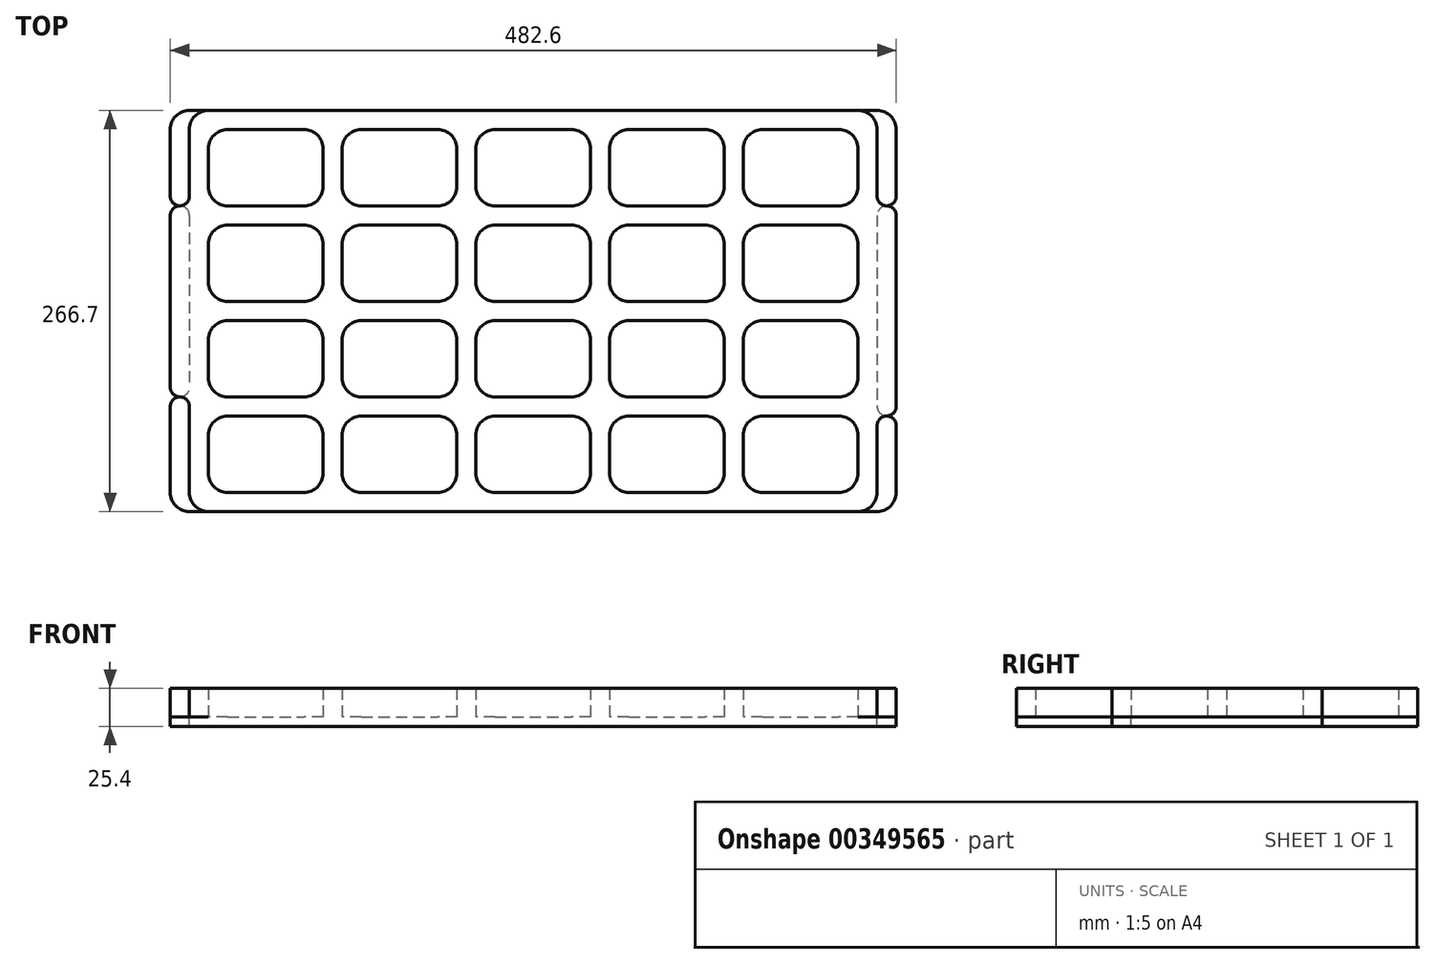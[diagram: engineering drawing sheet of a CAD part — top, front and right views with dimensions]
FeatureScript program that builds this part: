
annotation { "Feature Type Name" : "Feature", "Feature Type Description" : "" }
export const myFeature = defineFeature(function(context is Context, id is Id, definition is map)
    precondition{}
    {
        {
            var Q0;
            Q0=qCreatedBy(makeId("Top.planeOp"),FACE);
            var sketch = newSketch(context, id + "F0", { "sketchPlane" : qUnion([Q0])});
            skLineSegment(sketch, "E0.bottom", {"start": v(0, 0) * mm, "end": v(76.2, 0) * mm});
            skLineSegment(sketch, "E0.top", {"start": v(0, 50.8) * mm, "end": v(76.2, 50.8) * mm});
            skLineSegment(sketch, "E0.left", {"start": v(0, 0) * mm, "end": v(0, 50.8) * mm});
            skLineSegment(sketch, "E0.right", {"start": v(76.2, 0) * mm, "end": v(76.2, 50.8) * mm});
            skLineSegment(sketch, "E1.0.1.0", {"start": v(0, 114.3) * mm, "end": v(76.2, 114.3) * mm});
            skLineSegment(sketch, "E1.0.1.1", {"start": v(0, 63.5) * mm, "end": v(0, 114.3) * mm});
            skLineSegment(sketch, "E1.0.1.2", {"start": v(76.2, 63.5) * mm, "end": v(76.2, 114.3) * mm});
            skLineSegment(sketch, "E1.0.1.3", {"start": v(0, 63.5) * mm, "end": v(76.2, 63.5) * mm});
            skLineSegment(sketch, "E1.0.2.0", {"start": v(0, 177.8) * mm, "end": v(76.2, 177.8) * mm});
            skLineSegment(sketch, "E1.0.2.1", {"start": v(0, 127) * mm, "end": v(0, 177.8) * mm});
            skLineSegment(sketch, "E1.0.2.2", {"start": v(76.2, 127) * mm, "end": v(76.2, 177.8) * mm});
            skLineSegment(sketch, "E1.0.2.3", {"start": v(0, 127) * mm, "end": v(76.2, 127) * mm});
            skLineSegment(sketch, "E1.0.3.0", {"start": v(0, 241.3) * mm, "end": v(76.2, 241.3) * mm});
            skLineSegment(sketch, "E1.0.3.1", {"start": v(0, 190.5) * mm, "end": v(0, 241.3) * mm});
            skLineSegment(sketch, "E1.0.3.2", {"start": v(76.2, 190.5) * mm, "end": v(76.2, 241.3) * mm});
            skLineSegment(sketch, "E1.0.3.3", {"start": v(0, 190.5) * mm, "end": v(76.2, 190.5) * mm});
            skLineSegment(sketch, "E1.1.0.0", {"start": v(88.9, 50.8) * mm, "end": v(165.1, 50.8) * mm});
            skLineSegment(sketch, "E1.1.0.1", {"start": v(88.9, 0) * mm, "end": v(88.9, 50.8) * mm});
            skLineSegment(sketch, "E1.1.0.2", {"start": v(165.1, 0) * mm, "end": v(165.1, 50.8) * mm});
            skLineSegment(sketch, "E1.1.0.3", {"start": v(88.9, 0) * mm, "end": v(165.1, 0) * mm});
            skLineSegment(sketch, "E1.1.1.0", {"start": v(88.9, 114.3) * mm, "end": v(165.1, 114.3) * mm});
            skLineSegment(sketch, "E1.1.1.1", {"start": v(88.9, 63.5) * mm, "end": v(88.9, 114.3) * mm});
            skLineSegment(sketch, "E1.1.1.2", {"start": v(165.1, 63.5) * mm, "end": v(165.1, 114.3) * mm});
            skLineSegment(sketch, "E1.1.1.3", {"start": v(88.9, 63.5) * mm, "end": v(165.1, 63.5) * mm});
            skLineSegment(sketch, "E1.1.2.0", {"start": v(88.9, 177.8) * mm, "end": v(165.1, 177.8) * mm});
            skLineSegment(sketch, "E1.1.2.1", {"start": v(88.9, 127) * mm, "end": v(88.9, 177.8) * mm});
            skLineSegment(sketch, "E1.1.2.2", {"start": v(165.1, 127) * mm, "end": v(165.1, 177.8) * mm});
            skLineSegment(sketch, "E1.1.2.3", {"start": v(88.9, 127) * mm, "end": v(165.1, 127) * mm});
            skLineSegment(sketch, "E1.1.3.0", {"start": v(88.9, 241.3) * mm, "end": v(165.1, 241.3) * mm});
            skLineSegment(sketch, "E1.1.3.1", {"start": v(88.9, 190.5) * mm, "end": v(88.9, 241.3) * mm});
            skLineSegment(sketch, "E1.1.3.2", {"start": v(165.1, 190.5) * mm, "end": v(165.1, 241.3) * mm});
            skLineSegment(sketch, "E1.1.3.3", {"start": v(88.9, 190.5) * mm, "end": v(165.1, 190.5) * mm});
            skLineSegment(sketch, "E1.2.0.0", {"start": v(177.8, 50.8) * mm, "end": v(254, 50.8) * mm});
            skLineSegment(sketch, "E1.2.0.1", {"start": v(177.8, 0) * mm, "end": v(177.8, 50.8) * mm});
            skLineSegment(sketch, "E1.2.0.2", {"start": v(254, 0) * mm, "end": v(254, 50.8) * mm});
            skLineSegment(sketch, "E1.2.0.3", {"start": v(177.8, 0) * mm, "end": v(254, 0) * mm});
            skLineSegment(sketch, "E1.2.1.0", {"start": v(177.8, 114.3) * mm, "end": v(254, 114.3) * mm});
            skLineSegment(sketch, "E1.2.1.1", {"start": v(177.8, 63.5) * mm, "end": v(177.8, 114.3) * mm});
            skLineSegment(sketch, "E1.2.1.2", {"start": v(254, 63.5) * mm, "end": v(254, 114.3) * mm});
            skLineSegment(sketch, "E1.2.1.3", {"start": v(177.8, 63.5) * mm, "end": v(254, 63.5) * mm});
            skLineSegment(sketch, "E1.2.2.0", {"start": v(177.8, 177.8) * mm, "end": v(254, 177.8) * mm});
            skLineSegment(sketch, "E1.2.2.1", {"start": v(177.8, 127) * mm, "end": v(177.8, 177.8) * mm});
            skLineSegment(sketch, "E1.2.2.2", {"start": v(254, 127) * mm, "end": v(254, 177.8) * mm});
            skLineSegment(sketch, "E1.2.2.3", {"start": v(177.8, 127) * mm, "end": v(254, 127) * mm});
            skLineSegment(sketch, "E1.2.3.0", {"start": v(177.8, 241.3) * mm, "end": v(254, 241.3) * mm});
            skLineSegment(sketch, "E1.2.3.1", {"start": v(177.8, 190.5) * mm, "end": v(177.8, 241.3) * mm});
            skLineSegment(sketch, "E1.2.3.2", {"start": v(254, 190.5) * mm, "end": v(254, 241.3) * mm});
            skLineSegment(sketch, "E1.2.3.3", {"start": v(177.8, 190.5) * mm, "end": v(254, 190.5) * mm});
            skLineSegment(sketch, "E1.3.0.0", {"start": v(266.7, 50.8) * mm, "end": v(342.9, 50.8) * mm});
            skLineSegment(sketch, "E1.3.0.1", {"start": v(266.7, 0) * mm, "end": v(266.7, 50.8) * mm});
            skLineSegment(sketch, "E1.3.0.2", {"start": v(342.9, 0) * mm, "end": v(342.9, 50.8) * mm});
            skLineSegment(sketch, "E1.3.0.3", {"start": v(266.7, 0) * mm, "end": v(342.9, 0) * mm});
            skLineSegment(sketch, "E1.3.1.0", {"start": v(266.7, 114.3) * mm, "end": v(342.9, 114.3) * mm});
            skLineSegment(sketch, "E1.3.1.1", {"start": v(266.7, 63.5) * mm, "end": v(266.7, 114.3) * mm});
            skLineSegment(sketch, "E1.3.1.2", {"start": v(342.9, 63.5) * mm, "end": v(342.9, 114.3) * mm});
            skLineSegment(sketch, "E1.3.1.3", {"start": v(266.7, 63.5) * mm, "end": v(342.9, 63.5) * mm});
            skLineSegment(sketch, "E1.3.2.0", {"start": v(266.7, 177.8) * mm, "end": v(342.9, 177.8) * mm});
            skLineSegment(sketch, "E1.3.2.1", {"start": v(266.7, 127) * mm, "end": v(266.7, 177.8) * mm});
            skLineSegment(sketch, "E1.3.2.2", {"start": v(342.9, 127) * mm, "end": v(342.9, 177.8) * mm});
            skLineSegment(sketch, "E1.3.2.3", {"start": v(266.7, 127) * mm, "end": v(342.9, 127) * mm});
            skLineSegment(sketch, "E1.3.3.0", {"start": v(266.7, 241.3) * mm, "end": v(342.9, 241.3) * mm});
            skLineSegment(sketch, "E1.3.3.1", {"start": v(266.7, 190.5) * mm, "end": v(266.7, 241.3) * mm});
            skLineSegment(sketch, "E1.3.3.2", {"start": v(342.9, 190.5) * mm, "end": v(342.9, 241.3) * mm});
            skLineSegment(sketch, "E1.3.3.3", {"start": v(266.7, 190.5) * mm, "end": v(342.9, 190.5) * mm});
            skLineSegment(sketch, "E1.4.0.0", {"start": v(355.6, 50.8) * mm, "end": v(431.8, 50.8) * mm});
            skLineSegment(sketch, "E1.4.0.1", {"start": v(355.6, 0) * mm, "end": v(355.6, 50.8) * mm});
            skLineSegment(sketch, "E1.4.0.2", {"start": v(431.8, 0) * mm, "end": v(431.8, 50.8) * mm});
            skLineSegment(sketch, "E1.4.0.3", {"start": v(355.6, 0) * mm, "end": v(431.8, 0) * mm});
            skLineSegment(sketch, "E1.4.1.0", {"start": v(355.6, 114.3) * mm, "end": v(431.8, 114.3) * mm});
            skLineSegment(sketch, "E1.4.1.1", {"start": v(355.6, 63.5) * mm, "end": v(355.6, 114.3) * mm});
            skLineSegment(sketch, "E1.4.1.2", {"start": v(431.8, 63.5) * mm, "end": v(431.8, 114.3) * mm});
            skLineSegment(sketch, "E1.4.1.3", {"start": v(355.6, 63.5) * mm, "end": v(431.8, 63.5) * mm});
            skLineSegment(sketch, "E1.4.2.0", {"start": v(355.6, 177.8) * mm, "end": v(431.8, 177.8) * mm});
            skLineSegment(sketch, "E1.4.2.1", {"start": v(355.6, 127) * mm, "end": v(355.6, 177.8) * mm});
            skLineSegment(sketch, "E1.4.2.2", {"start": v(431.8, 127) * mm, "end": v(431.8, 177.8) * mm});
            skLineSegment(sketch, "E1.4.2.3", {"start": v(355.6, 127) * mm, "end": v(431.8, 127) * mm});
            skLineSegment(sketch, "E1.4.3.0", {"start": v(355.6, 241.3) * mm, "end": v(431.8, 241.3) * mm});
            skLineSegment(sketch, "E1.4.3.1", {"start": v(355.6, 190.5) * mm, "end": v(355.6, 241.3) * mm});
            skLineSegment(sketch, "E1.4.3.2", {"start": v(431.8, 190.5) * mm, "end": v(431.8, 241.3) * mm});
            skLineSegment(sketch, "E1.4.3.3", {"start": v(355.6, 190.5) * mm, "end": v(431.8, 190.5) * mm});
            skLineSegment(sketch, "E1.direction1", {"start": v(0, 0) * mm, "end": v(88.9, 0) * mm, "construction": true});
            skLineSegment(sketch, "E1.direction2", {"start": v(0, 0) * mm, "end": v(0, 63.5) * mm, "construction": true});
            skLineSegment(sketch, "E2.bottom", {"start": v(-12.7, 254) * mm, "end": v(444.5, 254) * mm});
            skLineSegment(sketch, "E2.top", {"start": v(-12.7, -12.7) * mm, "end": v(444.5, -12.7) * mm});
            skLineSegment(sketch, "E2.left", {"start": v(-12.7, 254) * mm, "end": v(-12.7, -12.7) * mm});
            skLineSegment(sketch, "E3", {"start": v(444.5, -12.7) * mm, "end": v(444.5, 254) * mm});
            skArc(sketch, "E4", {"start": v(450.85, 50.8) * mm, "mid": v(446.36, 48.94) * mm, "end": v(444.5, 44.45) * mm});
            skArc(sketch, "E5", {"start": v(444.5, 196.85) * mm, "mid": v(446.36, 192.36) * mm, "end": v(450.85, 190.5) * mm});
            skArc(sketch, "E6", {"start": v(457.2, 184.15) * mm, "mid": v(455.34, 188.64) * mm, "end": v(450.85, 190.5) * mm});
            skArc(sketch, "E7", {"start": v(450.85, 50.8) * mm, "mid": v(455.34, 52.66) * mm, "end": v(457.2, 57.15) * mm});
            skLineSegment(sketch, "E8", {"start": v(457.2, 184.15) * mm, "end": v(457.2, 57.15) * mm});
            skArc(sketch, "E9", {"start": v(-19.05, 190.5) * mm, "mid": v(-14.56, 192.36) * mm, "end": v(-12.7, 196.85) * mm});
            skArc(sketch, "E10", {"start": v(-19.05, 190.5) * mm, "mid": v(-23.54, 188.64) * mm, "end": v(-25.4, 184.15) * mm});
            skArc(sketch, "E11", {"start": v(-25.4, 69.85) * mm, "mid": v(-23.54, 65.36) * mm, "end": v(-19.05, 63.5) * mm});
            skArc(sketch, "E12", {"start": v(-12.7, 57.15) * mm, "mid": v(-14.56, 61.64) * mm, "end": v(-19.05, 63.5) * mm});
            skLineSegment(sketch, "E13", {"start": v(-25.4, 184.15) * mm, "end": v(-25.4, 69.85) * mm});
            skSolve(sketch);
        }
        {
            var Q0;
            Q0 = qSketchRegion(id + "F0", true);
            extrude(context, id + "F1", {"entities" : qUnion([Q0]), "depth" : 19.05 * mm});
        }
        {
            var Q0;
            Q0=makeQuery(id+"F1.opExtrude","SWEPT_EDGE",EDGE,{"disambiguationData":[OSD([sQuery(id+"F0.wireOp",EDGE,"E1.4.3.2"),sQuery(id+"F0.wireOp",EDGE,"E1.4.3.3")])]});
            var Q1;
            Q1=makeQuery(id+"F1.opExtrude","SWEPT_EDGE",EDGE,{"disambiguationData":[OSD([sQuery(id+"F0.wireOp",EDGE,"E1.4.2.2"),sQuery(id+"F0.wireOp",EDGE,"E1.4.2.3")])]});
            var Q2;
            Q2=makeQuery(id+"F1.opExtrude","SWEPT_EDGE",EDGE,{"disambiguationData":[OSD([sQuery(id+"F0.wireOp",EDGE,"E1.4.1.2"),sQuery(id+"F0.wireOp",EDGE,"E1.4.1.3")])]});
            var Q3;
            Q3=makeQuery(id+"F1.opExtrude","SWEPT_EDGE",EDGE,{"disambiguationData":[OSD([sQuery(id+"F0.wireOp",EDGE,"E1.4.0.2"),sQuery(id+"F0.wireOp",EDGE,"E1.4.0.3")])]});
            var Q4;
            Q4=makeQuery(id+"F1.opExtrude","SWEPT_EDGE",EDGE,{"disambiguationData":[OSD([sQuery(id+"F0.wireOp",EDGE,"E2.bottom"),sQuery(id+"F0.wireOp",EDGE,"E2.left")])]});
            var Q5;
            Q5=makeQuery(id+"F1.opExtrude","SWEPT_EDGE",EDGE,{"disambiguationData":[OSD([sQuery(id+"F0.wireOp",EDGE,"E1.0.3.2"),sQuery(id+"F0.wireOp",EDGE,"E1.0.3.3")])]});
            var Q6;
            Q6=makeQuery(id+"F1.opExtrude","SWEPT_EDGE",EDGE,{"disambiguationData":[OSD([sQuery(id+"F0.wireOp",EDGE,"E1.1.3.2"),sQuery(id+"F0.wireOp",EDGE,"E1.1.3.3")])]});
            var Q7;
            Q7=makeQuery(id+"F1.opExtrude","SWEPT_EDGE",EDGE,{"disambiguationData":[OSD([sQuery(id+"F0.wireOp",EDGE,"E1.2.3.2"),sQuery(id+"F0.wireOp",EDGE,"E1.2.3.3")])]});
            var Q8;
            Q8=makeQuery(id+"F1.opExtrude","SWEPT_EDGE",EDGE,{"disambiguationData":[OSD([sQuery(id+"F0.wireOp",EDGE,"E1.3.1.2"),sQuery(id+"F0.wireOp",EDGE,"E1.3.1.3")])]});
            var Q9;
            Q9=makeQuery(id+"F1.opExtrude","SWEPT_EDGE",EDGE,{"disambiguationData":[OSD([sQuery(id+"F0.wireOp",EDGE,"E1.3.0.2"),sQuery(id+"F0.wireOp",EDGE,"E1.3.0.3")])]});
            var Q10;
            Q10=makeQuery(id+"F1.opExtrude","SWEPT_EDGE",EDGE,{"disambiguationData":[OSD([sQuery(id+"F0.wireOp",EDGE,"E1.3.2.2"),sQuery(id+"F0.wireOp",EDGE,"E1.3.2.3")])]});
            var Q11;
            Q11=makeQuery(id+"F1.opExtrude","SWEPT_EDGE",EDGE,{"disambiguationData":[OSD([sQuery(id+"F0.wireOp",EDGE,"E1.3.3.2"),sQuery(id+"F0.wireOp",EDGE,"E1.3.3.3")])]});
            var Q12;
            Q12=makeQuery(id+"F1.opExtrude","SWEPT_EDGE",EDGE,{"disambiguationData":[OSD([sQuery(id+"F0.wireOp",EDGE,"E1.2.2.2"),sQuery(id+"F0.wireOp",EDGE,"E1.2.2.3")])]});
            var Q13;
            Q13=makeQuery(id+"F1.opExtrude","SWEPT_EDGE",EDGE,{"disambiguationData":[OSD([sQuery(id+"F0.wireOp",EDGE,"E1.2.1.2"),sQuery(id+"F0.wireOp",EDGE,"E1.2.1.3")])]});
            var Q14;
            Q14=makeQuery(id+"F1.opExtrude","SWEPT_EDGE",EDGE,{"disambiguationData":[OSD([sQuery(id+"F0.wireOp",EDGE,"E1.2.0.2"),sQuery(id+"F0.wireOp",EDGE,"E1.2.0.3")])]});
            var Q15;
            Q15=makeQuery(id+"F1.opExtrude","SWEPT_EDGE",EDGE,{"disambiguationData":[OSD([sQuery(id+"F0.wireOp",EDGE,"E1.1.0.2"),sQuery(id+"F0.wireOp",EDGE,"E1.1.0.3")])]});
            var Q16;
            Q16=makeQuery(id+"F1.opExtrude","SWEPT_EDGE",EDGE,{"disambiguationData":[OSD([sQuery(id+"F0.wireOp",EDGE,"E1.1.1.2"),sQuery(id+"F0.wireOp",EDGE,"E1.1.1.3")])]});
            var Q17;
            Q17=makeQuery(id+"F1.opExtrude","SWEPT_EDGE",EDGE,{"disambiguationData":[OSD([sQuery(id+"F0.wireOp",EDGE,"E1.1.2.2"),sQuery(id+"F0.wireOp",EDGE,"E1.1.2.3")])]});
            var Q18;
            Q18=makeQuery(id+"F1.opExtrude","SWEPT_EDGE",EDGE,{"disambiguationData":[OSD([sQuery(id+"F0.wireOp",EDGE,"E1.0.2.2"),sQuery(id+"F0.wireOp",EDGE,"E1.0.2.3")])]});
            var Q19;
            Q19=makeQuery(id+"F1.opExtrude","SWEPT_EDGE",EDGE,{"disambiguationData":[OSD([sQuery(id+"F0.wireOp",EDGE,"E1.0.1.2"),sQuery(id+"F0.wireOp",EDGE,"E1.0.1.3")])]});
            var Q20;
            Q20=makeQuery(id+"F1.opExtrude","SWEPT_EDGE",EDGE,{"disambiguationData":[OSD([sQuery(id+"F0.wireOp",EDGE,"E0.bottom"),sQuery(id+"F0.wireOp",EDGE,"E0.right")])]});
            var Q21;
            Q21=makeQuery(id+"F1.opExtrude","SWEPT_EDGE",EDGE,{"disambiguationData":[OSD([sQuery(id+"F0.wireOp",EDGE,"E1.4.0.1"),sQuery(id+"F0.wireOp",EDGE,"E1.4.0.3")])]});
            var Q22;
            Q22=makeQuery(id+"F1.opExtrude","SWEPT_EDGE",EDGE,{"disambiguationData":[OSD([sQuery(id+"F0.wireOp",EDGE,"E2.top"),sQuery(id+"F0.wireOp",EDGE,"E3")])]});
            var Q23;
            Q23=makeQuery(id+"F1.opExtrude","SWEPT_EDGE",EDGE,{"disambiguationData":[OSD([sQuery(id+"F0.wireOp",EDGE,"E2.bottom"),sQuery(id+"F0.wireOp",EDGE,"E3")])]});
            var Q24;
            Q24=makeQuery(id+"F1.opExtrude","SWEPT_EDGE",EDGE,{"disambiguationData":[OSD([sQuery(id+"F0.wireOp",EDGE,"E1.4.2.1"),sQuery(id+"F0.wireOp",EDGE,"E1.4.2.3")])]});
            var Q25;
            Q25=makeQuery(id+"F1.opExtrude","SWEPT_EDGE",EDGE,{"disambiguationData":[OSD([sQuery(id+"F0.wireOp",EDGE,"E1.4.1.1"),sQuery(id+"F0.wireOp",EDGE,"E1.4.1.3")])]});
            var Q26;
            Q26=makeQuery(id+"F1.opExtrude","SWEPT_EDGE",EDGE,{"disambiguationData":[OSD([sQuery(id+"F0.wireOp",EDGE,"E1.3.0.1"),sQuery(id+"F0.wireOp",EDGE,"E1.3.0.3")])]});
            var Q27;
            Q27=makeQuery(id+"F1.opExtrude","SWEPT_EDGE",EDGE,{"disambiguationData":[OSD([sQuery(id+"F0.wireOp",EDGE,"E1.3.1.1"),sQuery(id+"F0.wireOp",EDGE,"E1.3.1.3")])]});
            var Q28;
            Q28=makeQuery(id+"F1.opExtrude","SWEPT_EDGE",EDGE,{"disambiguationData":[OSD([sQuery(id+"F0.wireOp",EDGE,"E1.4.3.1"),sQuery(id+"F0.wireOp",EDGE,"E1.4.3.3")])]});
            var Q29;
            Q29=makeQuery(id+"F1.opExtrude","SWEPT_EDGE",EDGE,{"disambiguationData":[OSD([sQuery(id+"F0.wireOp",EDGE,"E1.2.0.1"),sQuery(id+"F0.wireOp",EDGE,"E1.2.0.3")])]});
            var Q30;
            Q30=makeQuery(id+"F1.opExtrude","SWEPT_EDGE",EDGE,{"disambiguationData":[OSD([sQuery(id+"F0.wireOp",EDGE,"E1.2.1.1"),sQuery(id+"F0.wireOp",EDGE,"E1.2.1.3")])]});
            var Q31;
            Q31=makeQuery(id+"F1.opExtrude","SWEPT_EDGE",EDGE,{"disambiguationData":[OSD([sQuery(id+"F0.wireOp",EDGE,"E1.2.2.1"),sQuery(id+"F0.wireOp",EDGE,"E1.2.2.3")])]});
            var Q32;
            Q32=makeQuery(id+"F1.opExtrude","SWEPT_EDGE",EDGE,{"disambiguationData":[OSD([sQuery(id+"F0.wireOp",EDGE,"E1.3.2.1"),sQuery(id+"F0.wireOp",EDGE,"E1.3.2.3")])]});
            var Q33;
            Q33=makeQuery(id+"F1.opExtrude","SWEPT_EDGE",EDGE,{"disambiguationData":[OSD([sQuery(id+"F0.wireOp",EDGE,"E1.3.3.1"),sQuery(id+"F0.wireOp",EDGE,"E1.3.3.3")])]});
            var Q34;
            Q34=makeQuery(id+"F1.opExtrude","SWEPT_EDGE",EDGE,{"disambiguationData":[OSD([sQuery(id+"F0.wireOp",EDGE,"E1.2.3.1"),sQuery(id+"F0.wireOp",EDGE,"E1.2.3.3")])]});
            var Q35;
            Q35=makeQuery(id+"F1.opExtrude","SWEPT_EDGE",EDGE,{"disambiguationData":[OSD([sQuery(id+"F0.wireOp",EDGE,"E1.1.3.1"),sQuery(id+"F0.wireOp",EDGE,"E1.1.3.3")])]});
            var Q36;
            Q36=makeQuery(id+"F1.opExtrude","SWEPT_EDGE",EDGE,{"disambiguationData":[OSD([sQuery(id+"F0.wireOp",EDGE,"E1.1.2.1"),sQuery(id+"F0.wireOp",EDGE,"E1.1.2.3")])]});
            var Q37;
            Q37=makeQuery(id+"F1.opExtrude","SWEPT_EDGE",EDGE,{"disambiguationData":[OSD([sQuery(id+"F0.wireOp",EDGE,"E1.1.1.1"),sQuery(id+"F0.wireOp",EDGE,"E1.1.1.3")])]});
            var Q38;
            Q38=makeQuery(id+"F1.opExtrude","SWEPT_EDGE",EDGE,{"disambiguationData":[OSD([sQuery(id+"F0.wireOp",EDGE,"E1.1.0.1"),sQuery(id+"F0.wireOp",EDGE,"E1.1.0.3")])]});
            var Q39;
            Q39=makeQuery(id+"F1.opExtrude","SWEPT_EDGE",EDGE,{"disambiguationData":[OSD([sQuery(id+"F0.wireOp",EDGE,"E0.bottom"),sQuery(id+"F0.wireOp",EDGE,"E0.left")])]});
            var Q40;
            Q40=makeQuery(id+"F1.opExtrude","SWEPT_EDGE",EDGE,{"disambiguationData":[OSD([sQuery(id+"F0.wireOp",EDGE,"E1.0.1.1"),sQuery(id+"F0.wireOp",EDGE,"E1.0.1.3")])]});
            var Q41;
            Q41=makeQuery(id+"F1.opExtrude","SWEPT_EDGE",EDGE,{"disambiguationData":[OSD([sQuery(id+"F0.wireOp",EDGE,"E1.0.2.1"),sQuery(id+"F0.wireOp",EDGE,"E1.0.2.3")])]});
            var Q42;
            Q42=makeQuery(id+"F1.opExtrude","SWEPT_EDGE",EDGE,{"disambiguationData":[OSD([sQuery(id+"F0.wireOp",EDGE,"E1.0.3.1"),sQuery(id+"F0.wireOp",EDGE,"E1.0.3.3")])]});
            var Q43;
            Q43=makeQuery(id+"F1.opExtrude","SWEPT_EDGE",EDGE,{"disambiguationData":[OSD([sQuery(id+"F0.wireOp",EDGE,"E1.0.3.0"),sQuery(id+"F0.wireOp",EDGE,"E1.0.3.1")])]});
            var Q44;
            Q44=makeQuery(id+"F1.opExtrude","SWEPT_EDGE",EDGE,{"disambiguationData":[OSD([sQuery(id+"F0.wireOp",EDGE,"E1.0.2.0"),sQuery(id+"F0.wireOp",EDGE,"E1.0.2.1")])]});
            var Q45;
            Q45=makeQuery(id+"F1.opExtrude","SWEPT_EDGE",EDGE,{"disambiguationData":[OSD([sQuery(id+"F0.wireOp",EDGE,"E1.0.1.0"),sQuery(id+"F0.wireOp",EDGE,"E1.0.1.1")])]});
            var Q46;
            Q46=makeQuery(id+"F1.opExtrude","SWEPT_EDGE",EDGE,{"disambiguationData":[OSD([sQuery(id+"F0.wireOp",EDGE,"E0.top"),sQuery(id+"F0.wireOp",EDGE,"E0.left")])]});
            var Q47;
            Q47=makeQuery(id+"F1.opExtrude","SWEPT_EDGE",EDGE,{"disambiguationData":[OSD([sQuery(id+"F0.wireOp",EDGE,"E1.1.0.0"),sQuery(id+"F0.wireOp",EDGE,"E1.1.0.1")])]});
            var Q48;
            Q48=makeQuery(id+"F1.opExtrude","SWEPT_EDGE",EDGE,{"disambiguationData":[OSD([sQuery(id+"F0.wireOp",EDGE,"E1.1.1.0"),sQuery(id+"F0.wireOp",EDGE,"E1.1.1.1")])]});
            var Q49;
            Q49=makeQuery(id+"F1.opExtrude","SWEPT_EDGE",EDGE,{"disambiguationData":[OSD([sQuery(id+"F0.wireOp",EDGE,"E1.1.2.0"),sQuery(id+"F0.wireOp",EDGE,"E1.1.2.1")])]});
            var Q50;
            Q50=makeQuery(id+"F1.opExtrude","SWEPT_EDGE",EDGE,{"disambiguationData":[OSD([sQuery(id+"F0.wireOp",EDGE,"E1.1.3.0"),sQuery(id+"F0.wireOp",EDGE,"E1.1.3.1")])]});
            var Q51;
            Q51=makeQuery(id+"F1.opExtrude","SWEPT_EDGE",EDGE,{"disambiguationData":[OSD([sQuery(id+"F0.wireOp",EDGE,"E1.2.3.0"),sQuery(id+"F0.wireOp",EDGE,"E1.2.3.1")])]});
            var Q52;
            Q52=makeQuery(id+"F1.opExtrude","SWEPT_EDGE",EDGE,{"disambiguationData":[OSD([sQuery(id+"F0.wireOp",EDGE,"E1.2.2.0"),sQuery(id+"F0.wireOp",EDGE,"E1.2.2.1")])]});
            var Q53;
            Q53=makeQuery(id+"F1.opExtrude","SWEPT_EDGE",EDGE,{"disambiguationData":[OSD([sQuery(id+"F0.wireOp",EDGE,"E1.2.1.0"),sQuery(id+"F0.wireOp",EDGE,"E1.2.1.1")])]});
            var Q54;
            Q54=makeQuery(id+"F1.opExtrude","SWEPT_EDGE",EDGE,{"disambiguationData":[OSD([sQuery(id+"F0.wireOp",EDGE,"E1.2.0.0"),sQuery(id+"F0.wireOp",EDGE,"E1.2.0.1")])]});
            var Q55;
            Q55=makeQuery(id+"F1.opExtrude","SWEPT_EDGE",EDGE,{"disambiguationData":[OSD([sQuery(id+"F0.wireOp",EDGE,"E1.3.3.0"),sQuery(id+"F0.wireOp",EDGE,"E1.3.3.1")])]});
            var Q56;
            Q56=makeQuery(id+"F1.opExtrude","SWEPT_EDGE",EDGE,{"disambiguationData":[OSD([sQuery(id+"F0.wireOp",EDGE,"E1.3.2.0"),sQuery(id+"F0.wireOp",EDGE,"E1.3.2.1")])]});
            var Q57;
            Q57=makeQuery(id+"F1.opExtrude","SWEPT_EDGE",EDGE,{"disambiguationData":[OSD([sQuery(id+"F0.wireOp",EDGE,"E1.3.1.0"),sQuery(id+"F0.wireOp",EDGE,"E1.3.1.1")])]});
            var Q58;
            Q58=makeQuery(id+"F1.opExtrude","SWEPT_EDGE",EDGE,{"disambiguationData":[OSD([sQuery(id+"F0.wireOp",EDGE,"E1.3.0.0"),sQuery(id+"F0.wireOp",EDGE,"E1.3.0.1")])]});
            var Q59;
            Q59=makeQuery(id+"F1.opExtrude","SWEPT_EDGE",EDGE,{"disambiguationData":[OSD([sQuery(id+"F0.wireOp",EDGE,"E1.4.0.0"),sQuery(id+"F0.wireOp",EDGE,"E1.4.0.1")])]});
            var Q60;
            Q60=makeQuery(id+"F1.opExtrude","SWEPT_EDGE",EDGE,{"disambiguationData":[OSD([sQuery(id+"F0.wireOp",EDGE,"E1.4.1.0"),sQuery(id+"F0.wireOp",EDGE,"E1.4.1.1")])]});
            var Q61;
            Q61=makeQuery(id+"F1.opExtrude","SWEPT_EDGE",EDGE,{"disambiguationData":[OSD([sQuery(id+"F0.wireOp",EDGE,"E1.4.2.0"),sQuery(id+"F0.wireOp",EDGE,"E1.4.2.1")])]});
            var Q62;
            Q62=makeQuery(id+"F1.opExtrude","SWEPT_EDGE",EDGE,{"disambiguationData":[OSD([sQuery(id+"F0.wireOp",EDGE,"E1.4.3.0"),sQuery(id+"F0.wireOp",EDGE,"E1.4.3.1")])]});
            var Q63;
            Q63=makeQuery(id+"F1.opExtrude","SWEPT_EDGE",EDGE,{"disambiguationData":[OSD([sQuery(id+"F0.wireOp",EDGE,"E1.4.3.0"),sQuery(id+"F0.wireOp",EDGE,"E1.4.3.2")])]});
            var Q64;
            Q64=makeQuery(id+"F1.opExtrude","SWEPT_EDGE",EDGE,{"disambiguationData":[OSD([sQuery(id+"F0.wireOp",EDGE,"E1.3.3.0"),sQuery(id+"F0.wireOp",EDGE,"E1.3.3.2")])]});
            var Q65;
            Q65=makeQuery(id+"F1.opExtrude","SWEPT_EDGE",EDGE,{"disambiguationData":[OSD([sQuery(id+"F0.wireOp",EDGE,"E1.2.3.0"),sQuery(id+"F0.wireOp",EDGE,"E1.2.3.2")])]});
            var Q66;
            Q66=makeQuery(id+"F1.opExtrude","SWEPT_EDGE",EDGE,{"disambiguationData":[OSD([sQuery(id+"F0.wireOp",EDGE,"E1.1.3.0"),sQuery(id+"F0.wireOp",EDGE,"E1.1.3.2")])]});
            var Q67;
            Q67=makeQuery(id+"F1.opExtrude","SWEPT_EDGE",EDGE,{"disambiguationData":[OSD([sQuery(id+"F0.wireOp",EDGE,"E1.0.3.0"),sQuery(id+"F0.wireOp",EDGE,"E1.0.3.2")])]});
            var Q68;
            Q68=makeQuery(id+"F1.opExtrude","SWEPT_EDGE",EDGE,{"disambiguationData":[OSD([sQuery(id+"F0.wireOp",EDGE,"E2.top"),sQuery(id+"F0.wireOp",EDGE,"E2.left")])]});
            var Q69;
            Q69=makeQuery(id+"F1.opExtrude","SWEPT_EDGE",EDGE,{"disambiguationData":[OSD([sQuery(id+"F0.wireOp",EDGE,"E1.0.2.0"),sQuery(id+"F0.wireOp",EDGE,"E1.0.2.2")])]});
            var Q70;
            Q70=makeQuery(id+"F1.opExtrude","SWEPT_EDGE",EDGE,{"disambiguationData":[OSD([sQuery(id+"F0.wireOp",EDGE,"E1.0.1.0"),sQuery(id+"F0.wireOp",EDGE,"E1.0.1.2")])]});
            var Q71;
            Q71=makeQuery(id+"F1.opExtrude","SWEPT_EDGE",EDGE,{"disambiguationData":[OSD([sQuery(id+"F0.wireOp",EDGE,"E0.top"),sQuery(id+"F0.wireOp",EDGE,"E0.right")])]});
            var Q72;
            Q72=makeQuery(id+"F1.opExtrude","SWEPT_EDGE",EDGE,{"disambiguationData":[OSD([sQuery(id+"F0.wireOp",EDGE,"E1.1.0.0"),sQuery(id+"F0.wireOp",EDGE,"E1.1.0.2")])]});
            var Q73;
            Q73=makeQuery(id+"F1.opExtrude","SWEPT_EDGE",EDGE,{"disambiguationData":[OSD([sQuery(id+"F0.wireOp",EDGE,"E1.1.1.0"),sQuery(id+"F0.wireOp",EDGE,"E1.1.1.2")])]});
            var Q74;
            Q74=makeQuery(id+"F1.opExtrude","SWEPT_EDGE",EDGE,{"disambiguationData":[OSD([sQuery(id+"F0.wireOp",EDGE,"E1.1.2.0"),sQuery(id+"F0.wireOp",EDGE,"E1.1.2.2")])]});
            var Q75;
            Q75=makeQuery(id+"F1.opExtrude","SWEPT_EDGE",EDGE,{"disambiguationData":[OSD([sQuery(id+"F0.wireOp",EDGE,"E1.3.2.0"),sQuery(id+"F0.wireOp",EDGE,"E1.3.2.2")])]});
            var Q76;
            Q76=makeQuery(id+"F1.opExtrude","SWEPT_EDGE",EDGE,{"disambiguationData":[OSD([sQuery(id+"F0.wireOp",EDGE,"E1.2.2.0"),sQuery(id+"F0.wireOp",EDGE,"E1.2.2.2")])]});
            var Q77;
            Q77=makeQuery(id+"F1.opExtrude","SWEPT_EDGE",EDGE,{"disambiguationData":[OSD([sQuery(id+"F0.wireOp",EDGE,"E1.2.1.0"),sQuery(id+"F0.wireOp",EDGE,"E1.2.1.2")])]});
            var Q78;
            Q78=makeQuery(id+"F1.opExtrude","SWEPT_EDGE",EDGE,{"disambiguationData":[OSD([sQuery(id+"F0.wireOp",EDGE,"E1.2.0.0"),sQuery(id+"F0.wireOp",EDGE,"E1.2.0.2")])]});
            var Q79;
            Q79=makeQuery(id+"F1.opExtrude","SWEPT_EDGE",EDGE,{"disambiguationData":[OSD([sQuery(id+"F0.wireOp",EDGE,"E1.3.1.0"),sQuery(id+"F0.wireOp",EDGE,"E1.3.1.2")])]});
            var Q80;
            Q80=makeQuery(id+"F1.opExtrude","SWEPT_EDGE",EDGE,{"disambiguationData":[OSD([sQuery(id+"F0.wireOp",EDGE,"E1.3.0.0"),sQuery(id+"F0.wireOp",EDGE,"E1.3.0.2")])]});
            var Q81;
            Q81=makeQuery(id+"F1.opExtrude","SWEPT_EDGE",EDGE,{"disambiguationData":[OSD([sQuery(id+"F0.wireOp",EDGE,"E1.4.0.0"),sQuery(id+"F0.wireOp",EDGE,"E1.4.0.2")])]});
            var Q82;
            Q82=makeQuery(id+"F1.opExtrude","SWEPT_EDGE",EDGE,{"disambiguationData":[OSD([sQuery(id+"F0.wireOp",EDGE,"E1.4.1.0"),sQuery(id+"F0.wireOp",EDGE,"E1.4.1.2")])]});
            var Q83;
            Q83=makeQuery(id+"F1.opExtrude","SWEPT_EDGE",EDGE,{"disambiguationData":[OSD([sQuery(id+"F0.wireOp",EDGE,"E1.4.2.0"),sQuery(id+"F0.wireOp",EDGE,"E1.4.2.2")])]});
            fillet(context, id + "F2", {"entities" : qUnion([Q0, Q1, Q2, Q3, Q4, Q5, Q6, Q7, Q8, Q9, Q10, Q11, Q12, Q13, Q14, Q15, Q16, Q17, Q18, Q19, Q20, Q21, Q22, Q23, Q24, Q25, Q26, Q27, Q28, Q29, Q30, Q31, Q32, Q33, Q34, Q35, Q36, Q37, Q38, Q39, Q40, Q41, Q42, Q43, Q44, Q45, Q46, Q47, Q48, Q49, Q50, Q51, Q52, Q53, Q54, Q55, Q56, Q57, Q58, Q59, Q60, Q61, Q62, Q63, Q64, Q65, Q66, Q67, Q68, Q69, Q70, Q71, Q72, Q73, Q74, Q75, Q76, Q77, Q78, Q79, Q80, Q81, Q82, Q83]), "radius" : 12.7 * mm, "tangentPropagation" : true, "allowEdgeOverflow" : false});
        }
        {
            var Q0;
            Q0=qCreatedBy(makeId("Top.planeOp"),FACE);
            var sketch = newSketch(context, id + "F3", { "sketchPlane" : qUnion([Q0])});
            skPoint(sketch, "E14.0", {"position": v(-12.7, 254) * mm});
            skPoint(sketch, "E15.0", {"position": v(-25.4, 184.15) * mm});
            skPoint(sketch, "E16.0", {"position": v(444.5, -12.7) * mm});
            skPoint(sketch, "E17.0", {"position": v(457.2, 57.15) * mm});
            skLineSegment(sketch, "E18", {"start": v(-25.4, -12.7) * mm, "end": v(-25.4, 254) * mm});
            skLineSegment(sketch, "E19", {"start": v(-25.4, 254) * mm, "end": v(457.2, 254) * mm});
            skLineSegment(sketch, "E20", {"start": v(457.2, 254) * mm, "end": v(457.2, -12.7) * mm});
            skLineSegment(sketch, "E21", {"start": v(457.2, -12.7) * mm, "end": v(-25.4, -12.7) * mm});
            skPoint(sketch, "E22.0", {"position": v(-19.05, 196.85) * mm});
            skPoint(sketch, "E23.0", {"position": v(-19.05, 184.15) * mm});
            skPoint(sketch, "E24.0", {"position": v(-19.05, 69.85) * mm});
            skPoint(sketch, "E25.0", {"position": v(-19.05, 57.15) * mm});
            skPoint(sketch, "E26.0", {"position": v(450.85, 44.45) * mm});
            skPoint(sketch, "E27.0", {"position": v(450.85, 57.15) * mm});
            skPoint(sketch, "E28.0", {"position": v(450.85, 184.15) * mm});
            skPoint(sketch, "E29.0", {"position": v(450.85, 196.85) * mm});
            skArc(sketch, "E30", {"start": v(-12.7, 184.15) * mm, "mid": v(-14.56, 188.64) * mm, "end": v(-19.05, 190.5) * mm});
            skArc(sketch, "E31", {"start": v(-25.4, 196.85) * mm, "mid": v(-23.54, 192.36) * mm, "end": v(-19.05, 190.5) * mm});
            skArc(sketch, "E32", {"start": v(-19.05, 63.5) * mm, "mid": v(-14.56, 65.36) * mm, "end": v(-12.7, 69.85) * mm});
            skArc(sketch, "E33", {"start": v(-19.05, 63.5) * mm, "mid": v(-23.54, 61.64) * mm, "end": v(-25.4, 57.15) * mm});
            skArc(sketch, "E34", {"start": v(457.2, 44.45) * mm, "mid": v(455.34, 48.94) * mm, "end": v(450.85, 50.8) * mm});
            skArc(sketch, "E35", {"start": v(444.5, 57.15) * mm, "mid": v(446.36, 52.66) * mm, "end": v(450.85, 50.8) * mm});
            skArc(sketch, "E36", {"start": v(450.85, 190.5) * mm, "mid": v(446.36, 188.64) * mm, "end": v(444.5, 184.15) * mm});
            skArc(sketch, "E37", {"start": v(450.85, 190.5) * mm, "mid": v(455.34, 192.36) * mm, "end": v(457.2, 196.85) * mm});
            skLineSegment(sketch, "E38", {"start": v(444.5, 184.15) * mm, "end": v(444.5, 57.15) * mm});
            skLineSegment(sketch, "E39", {"start": v(-12.7, 184.15) * mm, "end": v(-12.7, 69.85) * mm});
            skSolve(sketch);
        }
        {
            var Q0;
            {var subQ6=sQuery(id+"F3.wireOp",EDGE,"E19");Q0=makeQuery(id+"F3.imprint","IMPRINT",FACE,{"disambiguationData":[TD([[makeQuery(id+"F3.imprint","IMPRINT",EDGE,{"derivedFrom":subQ6}),-1.0]])]});}
            extrude(context, id + "F4", {"entities" : qUnion([Q0]), "operationType" : NewBodyOperationType.ADD, "oppositeDirection" : true, "depth" : 6.35 * mm});
        }
        {
            var Q0;
            Q0=makeQuery(id+"F4.opExtrude","SWEPT_EDGE",EDGE,{"disambiguationData":[OSD([sQuery(id+"F3.wireOp",EDGE,"E18"),sQuery(id+"F3.wireOp",EDGE,"E19")])]});
            var Q1;
            Q1=makeQuery(id+"F4.opExtrude","SWEPT_EDGE",EDGE,{"disambiguationData":[OSD([sQuery(id+"F3.wireOp",EDGE,"E18"),sQuery(id+"F3.wireOp",EDGE,"E21")])]});
            var Q2;
            Q2=makeQuery(id+"F4.opExtrude","SWEPT_EDGE",EDGE,{"disambiguationData":[OSD([sQuery(id+"F3.wireOp",EDGE,"E20"),sQuery(id+"F3.wireOp",EDGE,"E21")])]});
            var Q3;
            Q3=makeQuery(id+"F4.opExtrude","SWEPT_EDGE",EDGE,{"disambiguationData":[OSD([sQuery(id+"F3.wireOp",EDGE,"E19"),sQuery(id+"F3.wireOp",EDGE,"E20")])]});
            fillet(context, id + "F5", {"entities" : qUnion([Q0, Q1, Q2, Q3]), "radius" : 12.7 * mm, "tangentPropagation" : true, "allowEdgeOverflow" : false});
        }
    });
